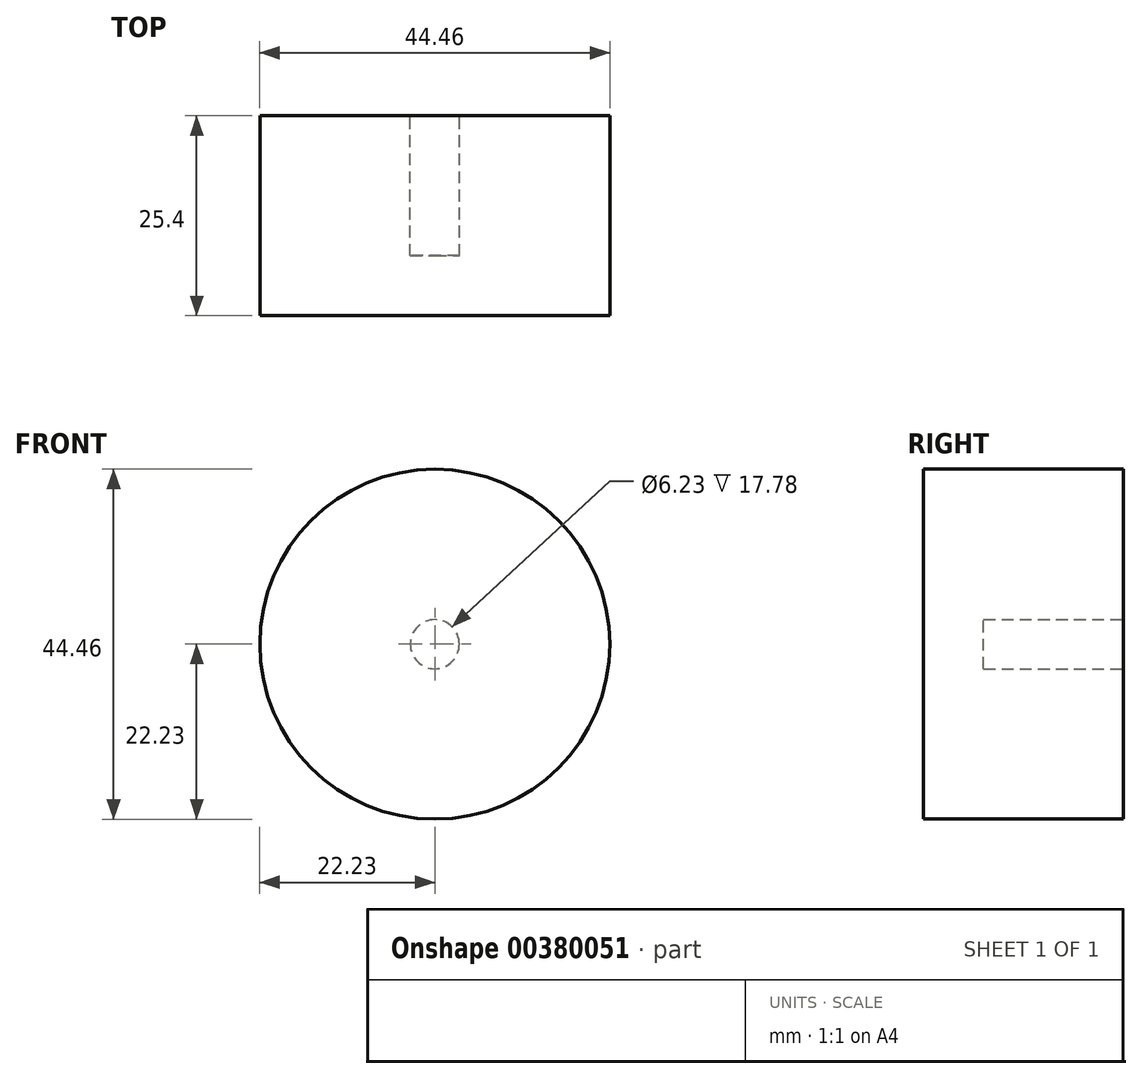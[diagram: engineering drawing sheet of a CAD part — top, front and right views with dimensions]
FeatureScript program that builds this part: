
annotation { "Feature Type Name" : "Feature", "Feature Type Description" : "" }
export const myFeature = defineFeature(function(context is Context, id is Id, definition is map)
    precondition{}
    {
        {
            var Q0;
            Q0=qCreatedBy(makeId("Front.planeOp"),FACE);
            var sketch = newSketch(context, id + "F0", { "sketchPlane" : qUnion([Q0])});
            skCircle(sketch, "E0", {"center": v(0, 0) * mm, "radius": 22.23 * mm});
            skSolve(sketch);
        }
        {
            var Q0;
            Q0=qCreatedBy(makeId("Top.planeOp"),FACE);
            var sketch = newSketch(context, id + "F1", { "sketchPlane" : qUnion([Q0])});
            skLineSegment(sketch, "E1.bottom", {"start": v(-3.9, 0) * mm, "end": v(4.18, 0) * mm});
            skLineSegment(sketch, "E1.top", {"start": v(-3.9, 5.85) * mm, "end": v(4.18, 5.85) * mm});
            skLineSegment(sketch, "E1.left", {"start": v(-3.9, 0) * mm, "end": v(-3.9, 5.85) * mm});
            skLineSegment(sketch, "E1.right", {"start": v(4.18, 0) * mm, "end": v(4.18, 5.85) * mm});
            skSolve(sketch);
        }
        {
            var Q0;
            Q0=qCreatedBy(makeId("Front.planeOp"),FACE);
            var sketch = newSketch(context, id + "F2", { "sketchPlane" : qUnion([Q0])});
            skLineSegment(sketch, "E2", {"start": v(-3.9, 20.36) * mm, "end": v(4.18, 20.36) * mm});
            skSolve(sketch);
        }
        {
            var Q0;
            Q0=qCreatedBy(makeId("Front.planeOp"),FACE);
            var sketch = newSketch(context, id + "F3", { "sketchPlane" : qUnion([Q0])});
            skLineSegment(sketch, "E3.bottom", {"start": v(4.18, 20.36) * mm, "end": v(-3.9, 20.36) * mm});
            skLineSegment(sketch, "E3.top", {"start": v(4.18, 25.4) * mm, "end": v(-3.9, 25.4) * mm});
            skLineSegment(sketch, "E3.left", {"start": v(4.18, 20.36) * mm, "end": v(4.18, 25.4) * mm});
            skLineSegment(sketch, "E3.right", {"start": v(-3.9, 20.36) * mm, "end": v(-3.9, 25.4) * mm});
            skSolve(sketch);
        }
        {
            var Q0;
            Q0=qCreatedBy(makeId("Front.planeOp"),FACE);
            var sketch = newSketch(context, id + "F4", { "sketchPlane" : qUnion([Q0])});
            skCircle(sketch, "E4", {"center": v(0, 0) * mm, "radius": 3.12 * mm});
            skSolve(sketch);
        }
        {
            var Q0;
            Q0=makeQuery(id+"F0.imprint","IMPRINT",FACE,{"disambiguationData":[TD([[makeQuery(id+"F0.imprint","IMPRINT",EDGE,{"derivedFrom":sQuery(id+"F0.wireOp",EDGE,"E0")}),1.0]])]});
            extrude(context, id + "F5", {"entities" : qUnion([Q0]), "depth" : 25.4 * mm});
        }
        {
            var Q0;
            Q0=makeQuery(id+"F4.imprint","IMPRINT",FACE,{"disambiguationData":[TD([[makeQuery(id+"F4.imprint","IMPRINT",EDGE,{"derivedFrom":sQuery(id+"F4.wireOp",EDGE,"E4")}),1.0]])]});
            extrude(context, id + "F6", {"entities" : qUnion([Q0]), "operationType" : NewBodyOperationType.REMOVE, "depth" : 17.78 * mm});
        }
    });
